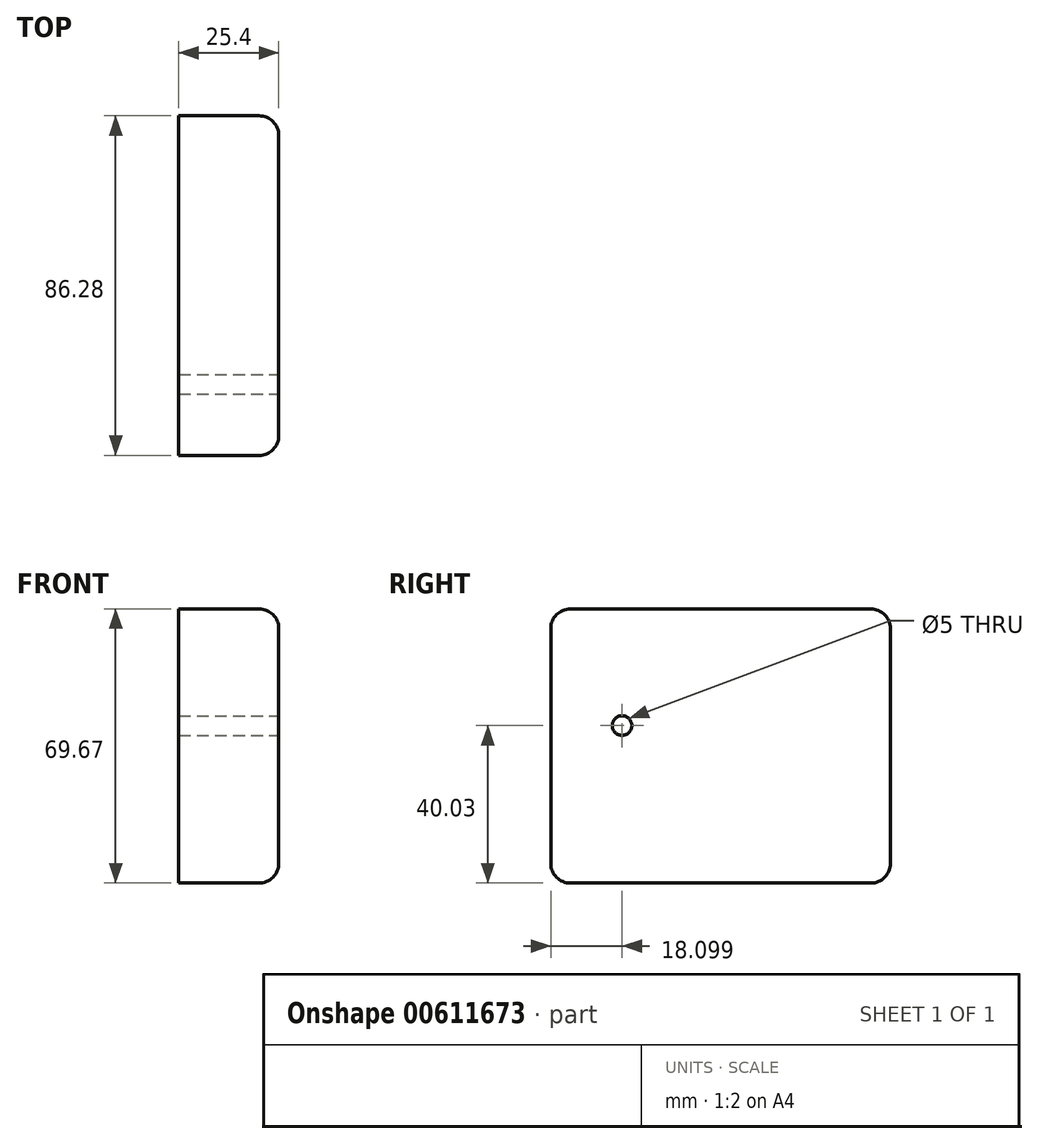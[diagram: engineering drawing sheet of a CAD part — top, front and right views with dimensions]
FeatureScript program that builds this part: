
annotation { "Feature Type Name" : "Feature", "Feature Type Description" : "" }
export const myFeature = defineFeature(function(context is Context, id is Id, definition is map)
    precondition{}
    {
        {
            var Q0;
            Q0=qCreatedBy(makeId("Right.planeOp"),FACE);
            var sketch = newSketch(context, id + "F0", { "sketchPlane" : qUnion([Q0])});
            skLineSegment(sketch, "E0.bottom", {"start": v(53.53, -40.03) * mm, "end": v(-32.75, -40.03) * mm});
            skLineSegment(sketch, "E0.top", {"start": v(53.53, 29.64) * mm, "end": v(-32.75, 29.64) * mm});
            skLineSegment(sketch, "E0.left", {"start": v(53.53, -40.03) * mm, "end": v(53.53, 29.64) * mm});
            skLineSegment(sketch, "E0.right", {"start": v(-32.75, -40.03) * mm, "end": v(-32.75, 29.64) * mm});
            skSolve(sketch);
        }
        {
            var Q0;
            Q0=makeQuery(id+"F0.imprint","IMPRINT",FACE,{"disambiguationData":[TD([[makeQuery(id+"F0.imprint","IMPRINT",EDGE,{"derivedFrom":sQuery(id+"F0.wireOp",EDGE,"E0.bottom")}),-1.0]])]});
            extrude(context, id + "F1", {"entities" : qUnion([Q0]), "depth" : 25.4 * mm, "offsetDistance" : 25.4 * mm});
        }
        {
            var Q0;
            Q0=makeQuery(id+"F1.opExtrude","CAP_EDGE",EDGE,{"disambiguationData":[OSD([sQuery(id+"F0.wireOp",EDGE,"E0.bottom")])],"isStart":false});
            fillet(context, id + "F2", {"entities" : qUnion([Q0]), "radius" : 5.08 * mm, "tangentPropagation" : true, "allowEdgeOverflow" : false});
        }
        {
            var Q0;
            Q0=makeQuery(id+"F1.opExtrude","CAP_EDGE",EDGE,{"disambiguationData":[OSD([sQuery(id+"F0.wireOp",EDGE,"E0.left")])],"isStart":false});
            fillet(context, id + "F3", {"entities" : qUnion([Q0]), "radius" : 5 * mm, "tangentPropagation" : true, "allowEdgeOverflow" : false});
        }
        {
            var Q0;
            Q0=makeQuery(id+"F1.opExtrude","CAP_EDGE",EDGE,{"disambiguationData":[OSD([sQuery(id+"F0.wireOp",EDGE,"E0.top")])],"isStart":false});
            fillet(context, id + "F4", {"entities" : qUnion([Q0]), "radius" : 5 * mm, "tangentPropagation" : true, "allowEdgeOverflow" : false});
        }
        {
            var Q0;
            Q0=makeQuery(id+"F1.opExtrude","CAP_EDGE",EDGE,{"disambiguationData":[OSD([sQuery(id+"F0.wireOp",EDGE,"E0.right")])],"isStart":false});
            fillet(context, id + "F5", {"entities" : qUnion([Q0]), "radius" : 5 * mm, "tangentPropagation" : true, "allowEdgeOverflow" : false});
        }
        {
            var Q0;
            Q0=makeQuery(id+"F1.opExtrude","CAP_FACE",FACE,{"disambiguationData":[OSD([sQuery(id+"F0.wireOp",EDGE,"E0.bottom"),sQuery(id+"F0.wireOp",EDGE,"E0.top"),sQuery(id+"F0.wireOp",EDGE,"E0.left"),sQuery(id+"F0.wireOp",EDGE,"E0.right")])],"isStart":false});
            var sketch = newSketch(context, id + "F6", { "sketchPlane" : qUnion([Q0])});
            skCircle(sketch, "E1", {"center": v(-14.65, 0) * mm, "radius": 14.11 * mm});
            skCircle(sketch, "E2", {"center": v(-14.65, 0) * mm, "radius": 24.64 * mm, "construction": true});
            skSolve(sketch);
        }
        {
            var Q0;
            Q0=sQuery(id+"F6.wireOp",VERTEX,"E1.center");
            var Q1;
            Q1=makeQuery(id+"F1.opExtrude","SWEPT_BODY",BODY,{"disambiguationData":[OSD([sQuery(id+"F0.wireOp",EDGE,"E0.bottom"),sQuery(id+"F0.wireOp",EDGE,"E0.top"),sQuery(id+"F0.wireOp",EDGE,"E0.left"),sQuery(id+"F0.wireOp",EDGE,"E0.right")])]});
            hole(context, id + "F7", {"style" : HoleStyle.SIMPLE, "endStyle" : HoleEndStyle.THROUGH, "holeDiameter" : 5 * mm, "majorDiameter" : 5 * mm, "isTappedThrough" : true, "tappedDepth" : 12 * mm, "tapClearance" : 3, "locations" : qUnion([Q0]), "scope" : qUnion([Q1])});
        }
    });
